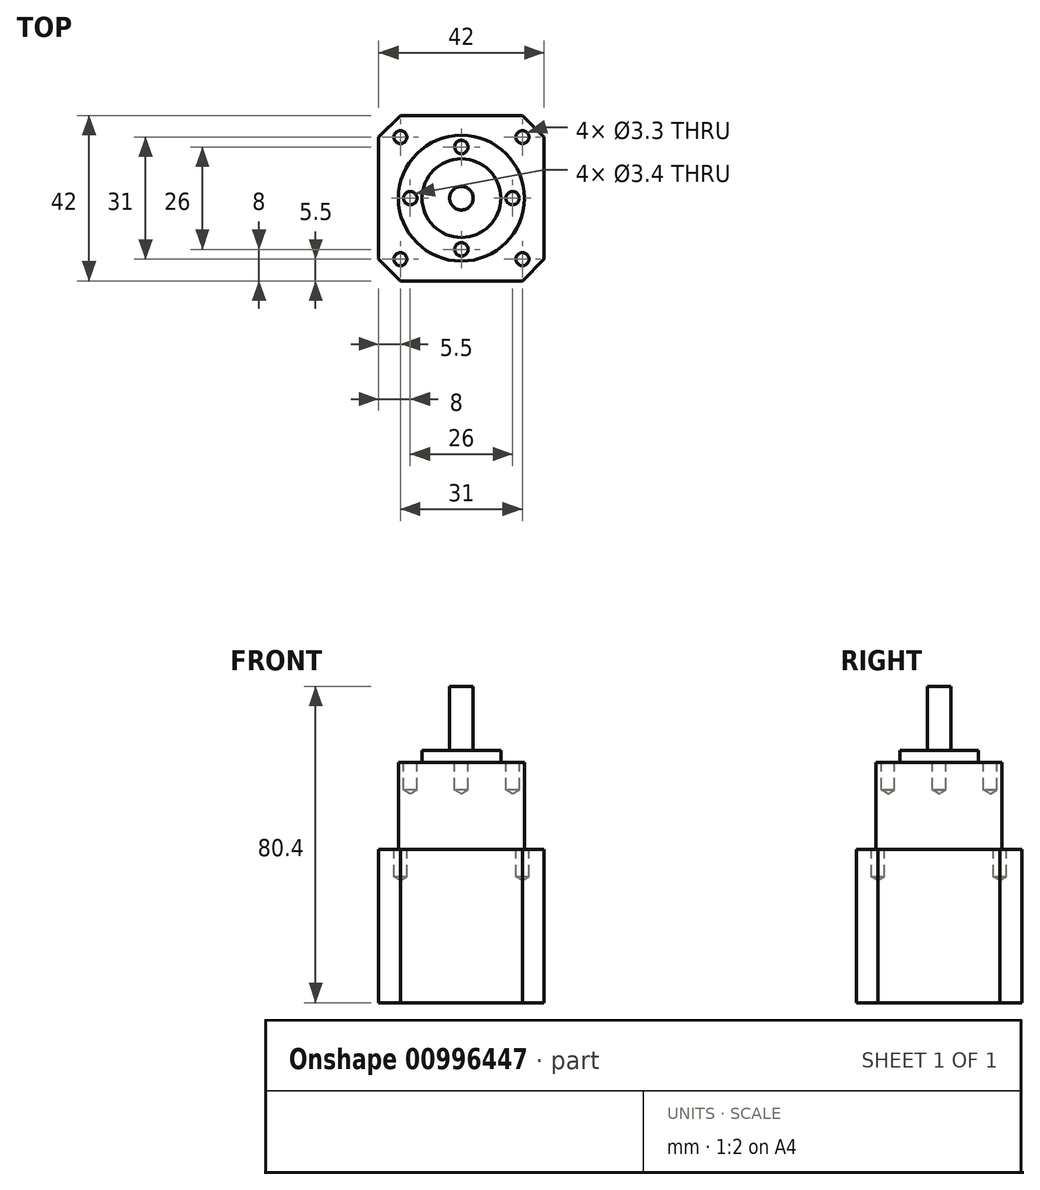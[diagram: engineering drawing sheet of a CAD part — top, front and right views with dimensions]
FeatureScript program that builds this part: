
annotation { "Feature Type Name" : "Feature", "Feature Type Description" : "" }
export const myFeature = defineFeature(function(context is Context, id is Id, definition is map)
    precondition{}
    {
        {
            var Q0;
            Q0=qCreatedBy(makeId("Top.planeOp"),FACE);
            var sketch = newSketch(context, id + "F0", { "sketchPlane" : qUnion([Q0])});
            skLineSegment(sketch, "E0.bottom", {"start": v(-21, 21) * mm, "end": v(21, 21) * mm});
            skLineSegment(sketch, "E0.top", {"start": v(-21, -21) * mm, "end": v(21, -21) * mm});
            skLineSegment(sketch, "E0.left", {"start": v(-21, 21) * mm, "end": v(-21, -21) * mm});
            skLineSegment(sketch, "E0.right", {"start": v(21, 21) * mm, "end": v(21, -21) * mm});
            skPoint(sketch, "E0.middle", {"position": v(0, 0) * mm});
            skSolve(sketch);
        }
        {
            var Q0;
            Q0 = qSketchRegion(id + "F0", true);
            extrude(context, id + "F1", {"entities" : qUnion([Q0]), "depth" : 39 * mm, "offsetDistance" : 25 * mm});
        }
        {
            var Q0;
            Q0=makeQuery(id+"F1.opExtrude","CAP_FACE",FACE,{"disambiguationData":[OSD([sQuery(id+"F0.wireOp",EDGE,"E0.bottom"),sQuery(id+"F0.wireOp",EDGE,"E0.top"),sQuery(id+"F0.wireOp",EDGE,"E0.left"),sQuery(id+"F0.wireOp",EDGE,"E0.right")])],"isStart":false});
            var sketch = newSketch(context, id + "F2", { "sketchPlane" : qUnion([Q0])});
            skCircle(sketch, "E1", {"center": v(0, 0) * mm, "radius": 16 * mm});
            skSolve(sketch);
        }
        {
            var Q0;
            Q0=makeQuery(id+"F2.imprint","IMPRINT",FACE,{"disambiguationData":[TD([[makeQuery(id+"F2.imprint","IMPRINT",EDGE,{"derivedFrom":sQuery(id+"F2.wireOp",EDGE,"E1")}),1.0]])]});
            extrude(context, id + "F3", {"entities" : qUnion([Q0]), "operationType" : NewBodyOperationType.ADD, "depth" : 22.1 * mm, "offsetDistance" : 25 * mm});
        }
        {
            var Q0;
            Q0=makeQuery(id+"F3.opExtrude","CAP_FACE",FACE,{"disambiguationData":[OSD([sQuery(id+"F2.wireOp",EDGE,"E1")])],"isStart":false});
            var sketch = newSketch(context, id + "F4", { "sketchPlane" : qUnion([Q0])});
            skCircle(sketch, "E2", {"center": v(0, 0) * mm, "radius": 10 * mm});
            skSolve(sketch);
        }
        {
            var Q0;
            Q0 = qSketchRegion(id + "F4", true);
            extrude(context, id + "F5", {"entities" : qUnion([Q0]), "operationType" : NewBodyOperationType.ADD, "depth" : 3 * mm, "offsetDistance" : 25 * mm});
        }
        {
            var Q0;
            Q0=makeQuery(id+"F5.opExtrude","CAP_FACE",FACE,{"disambiguationData":[OSD([sQuery(id+"F4.wireOp",EDGE,"E2")])],"isStart":false});
            var sketch = newSketch(context, id + "F6", { "sketchPlane" : qUnion([Q0])});
            skCircle(sketch, "E3", {"center": v(0, 0) * mm, "radius": 3 * mm});
            skSolve(sketch);
        }
        {
            var Q0;
            Q0 = qSketchRegion(id + "F6", true);
            extrude(context, id + "F7", {"entities" : qUnion([Q0]), "operationType" : NewBodyOperationType.ADD, "depth" : 16.3 * mm, "offsetDistance" : 25 * mm});
        }
        {
            var Q0;
            Q0=makeQuery(id+"F1.opExtrude","SWEPT_EDGE",EDGE,{"disambiguationData":[OSD([sQuery(id+"F0.wireOp",EDGE,"E0.bottom"),sQuery(id+"F0.wireOp",EDGE,"E0.left")])]});
            var Q1;
            Q1=makeQuery(id+"F1.opExtrude","SWEPT_EDGE",EDGE,{"disambiguationData":[OSD([sQuery(id+"F0.wireOp",EDGE,"E0.bottom"),sQuery(id+"F0.wireOp",EDGE,"E0.right")])]});
            var Q2;
            Q2=makeQuery(id+"F1.opExtrude","SWEPT_EDGE",EDGE,{"disambiguationData":[OSD([sQuery(id+"F0.wireOp",EDGE,"E0.top"),sQuery(id+"F0.wireOp",EDGE,"E0.right")])]});
            var Q3;
            Q3=makeQuery(id+"F1.opExtrude","SWEPT_EDGE",EDGE,{"disambiguationData":[OSD([sQuery(id+"F0.wireOp",EDGE,"E0.top"),sQuery(id+"F0.wireOp",EDGE,"E0.left")])]});
            chamfer(context, id + "F8", {"entities" : qUnion([Q0, Q1, Q2, Q3]), "width" : 5.5 * mm, "tangentPropagation" : true});
        }
        {
            var Q0;
            Q0=makeQuery(id+"F1.opExtrude","CAP_FACE",FACE,{"disambiguationData":[OSD([sQuery(id+"F0.wireOp",EDGE,"E0.bottom"),sQuery(id+"F0.wireOp",EDGE,"E0.top"),sQuery(id+"F0.wireOp",EDGE,"E0.left"),sQuery(id+"F0.wireOp",EDGE,"E0.right")])],"isStart":false});
            var sketch = newSketch(context, id + "F9", { "sketchPlane" : qUnion([Q0])});
            skPoint(sketch, "E4", {"position": v(-15.5, 15.5) * mm});
            skPoint(sketch, "E5", {"position": v(-15.5, -15.5) * mm});
            skPoint(sketch, "E6", {"position": v(15.5, -15.5) * mm});
            skPoint(sketch, "E7", {"position": v(15.5, 15.5) * mm});
            skLineSegment(sketch, "E8.bottom", {"start": v(-15.5, -15.5) * mm, "end": v(15.5, -15.5) * mm, "construction": true});
            skLineSegment(sketch, "E8.top", {"start": v(-15.5, 15.5) * mm, "end": v(15.5, 15.5) * mm, "construction": true});
            skLineSegment(sketch, "E8.left", {"start": v(-15.5, -15.5) * mm, "end": v(-15.5, 15.5) * mm, "construction": true});
            skLineSegment(sketch, "E8.right", {"start": v(15.5, -15.5) * mm, "end": v(15.5, 15.5) * mm, "construction": true});
            skLineSegment(sketch, "E9", {"start": v(-15.5, 15.5) * mm, "end": v(15.5, -15.5) * mm, "construction": true});
            skLineSegment(sketch, "E10", {"start": v(-15.5, -15.5) * mm, "end": v(15.5, 15.5) * mm, "construction": true});
            skPoint(sketch, "E11", {"position": v(0, 0) * mm});
            skSolve(sketch);
        }
        {
            var Q0;
            Q0=sQuery(id+"F9.wireOp",VERTEX,"E4");
            var Q1;
            Q1=sQuery(id+"F9.wireOp",VERTEX,"E7");
            var Q2;
            Q2=sQuery(id+"F9.wireOp",VERTEX,"E6");
            var Q3;
            Q3=sQuery(id+"F9.wireOp",VERTEX,"E5");
            var Q4;
            Q4=makeQuery(id+"F1.opExtrude","SWEPT_BODY",BODY,{"disambiguationData":[OSD([sQuery(id+"F0.wireOp",EDGE,"E0.bottom"),sQuery(id+"F0.wireOp",EDGE,"E0.top"),sQuery(id+"F0.wireOp",EDGE,"E0.left"),sQuery(id+"F0.wireOp",EDGE,"E0.right")])]});
            hole(context, id + "F10", {"style" : HoleStyle.SIMPLE, "endStyle" : HoleEndStyle.BLIND, "standardTappedOrClearance" : lookupTablePath({ "fit" : "Standard", "standard" : "ISO", "size" : "M3", "type" : "Clearance" }), "standardBlindInLast" : lookupTablePath({ "fit" : "Standard", "standard" : "ISO", "size" : "M3", "type" : "Clearance" }), "holeDiameter" : 3.3 * mm, "majorDiameter" : 5 * mm, "holeDepth" : 7 * mm, "isTappedThrough" : true, "tappedDepth" : 5.5 * mm, "tapClearance" : 3, "locations" : qUnion([Q0, Q1, Q2, Q3]), "scope" : qUnion([Q4])});
        }
        {
            var Q0;
            Q0=makeQuery(id+"F3.opExtrude","CAP_FACE",FACE,{"disambiguationData":[OSD([sQuery(id+"F2.wireOp",EDGE,"E1")])],"isStart":false});
            var sketch = newSketch(context, id + "F11", { "sketchPlane" : qUnion([Q0])});
            skCircle(sketch, "E12", {"center": v(0, 0) * mm, "radius": 13 * mm, "construction": true});
            skPoint(sketch, "E13", {"position": v(13, 0) * mm});
            skPoint(sketch, "E14", {"position": v(0, 13) * mm});
            skPoint(sketch, "E15", {"position": v(-13, 0) * mm});
            skPoint(sketch, "E16", {"position": v(0, -13) * mm});
            skSolve(sketch);
        }
        {
            var Q0;
            Q0=sQuery(id+"F11.wireOp",VERTEX,"E14");
            var Q1;
            Q1=sQuery(id+"F11.wireOp",VERTEX,"E15");
            var Q2;
            Q2=sQuery(id+"F11.wireOp",VERTEX,"E16");
            var Q3;
            Q3=sQuery(id+"F11.wireOp",VERTEX,"E13");
            var Q4;
            Q4=makeQuery(id+"F1.opExtrude","SWEPT_BODY",BODY,{"disambiguationData":[OSD([sQuery(id+"F0.wireOp",EDGE,"E0.bottom"),sQuery(id+"F0.wireOp",EDGE,"E0.top"),sQuery(id+"F0.wireOp",EDGE,"E0.left"),sQuery(id+"F0.wireOp",EDGE,"E0.right")])]});
            hole(context, id + "F12", {"style" : HoleStyle.SIMPLE, "endStyle" : HoleEndStyle.BLIND, "standardTappedOrClearance" : lookupTablePath({ "fit" : "Normal", "standard" : "ISO", "size" : "M3", "type" : "Clearance" }), "standardBlindInLast" : lookupTablePath({ "fit" : "Normal", "standard" : "ISO", "engagement" : "75%", "pitch" : "0.5 mm", "size" : "M3", "type" : "Clearance & tapped" }), "holeDiameter" : 3.4 * mm, "majorDiameter" : 5 * mm, "holeDepth" : 7 * mm, "isTappedThrough" : true, "tappedDepth" : 5.5 * mm, "tapClearance" : 3, "locations" : qUnion([Q0, Q1, Q2, Q3]), "scope" : qUnion([Q4])});
        }
    });
